# Revit family: Deckel für Kreuzung Magic
name_source: partatom
category: Generic Models
revit_build: Autodesk Revit 2015 (Build: 20140606_1530(x64)
units: mm (PartAtom-declared; Revit-internal decimal feet)

## types (13) — shared parameters
Manufacturer = OBO Bettermann
URL = http://www.obo-bettermann.com
Width = 1 mm  [stored 0.00328084 ft]
Width 1 = 2 mm  [stored 0.00656168 ft]

## per-type parameters (varying)
| type | GTIN | Height | Height 1 | Height 3 | Manufacturer Art.No. | Material |
| DFKM 100 FS | 4012195931256 | 198 mm  [stored 0.649606 ft] | 99 mm  [stored 0.324803 ft] | 52 mm | 7138930 | Strip-galvanised |
| DFKM 150 FS | 40121959312636 | 248 mm  [stored 0.813648 ft] | 124 mm  [stored 0.406824 ft] | 77 mm | 7138932 | Strip-galvanised |
| DFKM 200 FS | 40121959312708 | 298 mm  [stored 0.97769 ft] | 149 mm  [stored 0.488845 ft] | 102 mm | 7138934 | Strip-galvanised |
| DFKM 300 FS | 401219593128712 | 398 mm  [stored 1.30577 ft] | 199 mm  [stored 0.652887 ft] | 152 mm | 7138936 | Strip-galvanised |
| DFKM 400 FS | 401219593129416 | 498 mm  [stored 1.63386 ft] | 249 mm  [stored 0.816929 ft] | 202 mm | 7138938 | Strip-galvanised |
| DFKM 500 FS | 401219593130020 | 598 mm  [stored 1.96194 ft] | 299 mm  [stored 0.980971 ft] | 252 mm | 7138940 | Strip-galvanised |
| DFKM 600 FS | 401219593131724 | 698 mm  [stored 2.29003 ft] | 349 mm  [stored 1.14501 ft] | 302 mm | 7138942 | Strip-galvanised |
| DFKM 100 DD | 4012195931324 | 198 mm  [stored 0.649606 ft] | 99 mm  [stored 0.324803 ft] | 52 mm | 7138970 | Strip galvanised zinc/aluminium, Double Dip |
| DFKM 200 DD | 4012195931362 | 298 mm  [stored 0.97769 ft] | 149 mm  [stored 0.488845 ft] | 102 mm | 7138974 | Strip galvanised zinc/aluminium, Double Dip |
| DFKM 300 DD | 4012195931379 | 398 mm  [stored 1.30577 ft] | 199 mm  [stored 0.652887 ft] | 152 mm | 7138976 | Strip galvanised zinc/aluminium, Double Dip |
| DFKM 400 DD | 4012195931386 | 498 mm  [stored 1.63386 ft] | 249 mm  [stored 0.816929 ft] | 202 mm | 7138978 | Strip galvanised zinc/aluminium, Double Dip |
| DFKM 500 DD | 4012195931393 | 598 mm  [stored 1.96194 ft] | 299 mm  [stored 0.980971 ft] | 252 mm | 7138980 | Strip galvanised zinc/aluminium, Double Dip |
| DFKM 600 DD | 4012195931409 | 698 mm  [stored 2.29003 ft] | 349 mm  [stored 1.14501 ft] | 302 mm | 7138982 | Strip galvanised zinc/aluminium, Double Dip |

note: column(s) folded — value = type name in every type: Article Type

note: [stored X ft] marks values corroborated as IEEE doubles in the binary element streams (Revit-internal decimal feet)

## geometry (parser evidence)
native form markers: Sweep x1
no freeform markers — native parametric forms only
